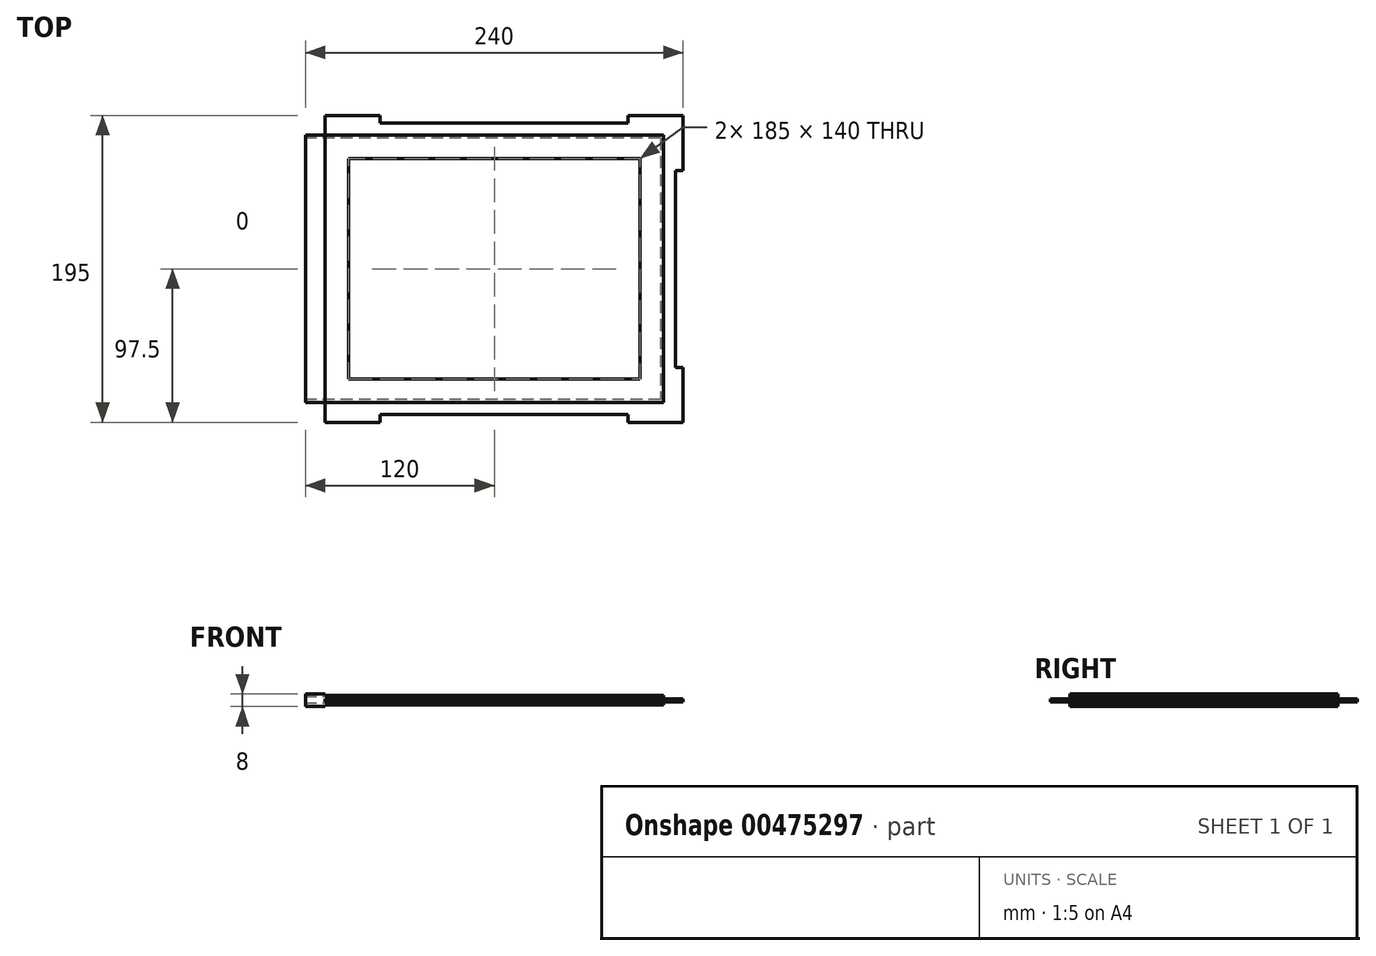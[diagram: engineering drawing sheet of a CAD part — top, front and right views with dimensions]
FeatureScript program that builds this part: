
annotation { "Feature Type Name" : "Feature", "Feature Type Description" : "" }
export const myFeature = defineFeature(function(context is Context, id is Id, definition is map)
    precondition{}
    {
        {
            var Q0;
            Q0=qCreatedBy(makeId("Top.planeOp"),FACE);
            var sketch = newSketch(context, id + "F0", { "sketchPlane" : qUnion([Q0])});
            skLineSegment(sketch, "E0.bottom", {"start": v(92.5, 70) * mm, "end": v(-92.5, 70) * mm});
            skLineSegment(sketch, "E0.top", {"start": v(92.5, -70) * mm, "end": v(-92.5, -70) * mm});
            skLineSegment(sketch, "E0.left", {"start": v(92.5, 70) * mm, "end": v(92.5, -70) * mm});
            skLineSegment(sketch, "E0.right", {"start": v(-92.5, 70) * mm, "end": v(-92.5, -70) * mm});
            skPoint(sketch, "E0.middle", {"position": v(0, 0) * mm});
            skLineSegment(sketch, "E1.bottom", {"start": v(120, 97.5) * mm, "end": v(85, 97.5) * mm});
            skLineSegment(sketch, "E1.top", {"start": v(120, -97.5) * mm, "end": v(85, -97.5) * mm});
            skLineSegment(sketch, "E1.left", {"start": v(120, 97.5) * mm, "end": v(120, 62.5) * mm});
            skLineSegment(sketch, "E1.right", {"start": v(-120, 85) * mm, "end": v(-120, -85) * mm});
            skLineSegment(sketch, "E2.bottom", {"start": v(107.5, -85) * mm, "end": v(-107.5, -85) * mm});
            skLineSegment(sketch, "E2.top", {"start": v(107.5, 85) * mm, "end": v(-107.5, 85) * mm});
            skLineSegment(sketch, "E2.left", {"start": v(107.5, -85) * mm, "end": v(107.5, 85) * mm});
            skLineSegment(sketch, "E2.right", {"start": v(-107.5, -85) * mm, "end": v(-107.5, 85) * mm});
            skLineSegment(sketch, "E3", {"start": v(-107.5, 85) * mm, "end": v(-120, 85) * mm});
            skLineSegment(sketch, "E4", {"start": v(-107.5, 85) * mm, "end": v(-107.5, 97.5) * mm});
            skPoint(sketch, "E5.orphan", {"position": v(-120, 97.5) * mm});
            skLineSegment(sketch, "E6", {"start": v(-107.5, -85) * mm, "end": v(-120, -85) * mm});
            skLineSegment(sketch, "E7", {"start": v(-107.5, -85) * mm, "end": v(-107.5, -97.5) * mm});
            skPoint(sketch, "E8.orphan", {"position": v(-120, -97.5) * mm});
            skLineSegment(sketch, "E9", {"start": v(-72.5, 97.5) * mm, "end": v(-72.5, 92.5) * mm});
            skLineSegment(sketch, "E10", {"start": v(-72.5, 92.5) * mm, "end": v(85, 92.5) * mm});
            skLineSegment(sketch, "E11", {"start": v(85, 92.5) * mm, "end": v(85, 97.5) * mm});
            skLineSegment(sketch, "E12", {"start": v(-72.5, -97.5) * mm, "end": v(-72.5, -92.5) * mm});
            skLineSegment(sketch, "E13", {"start": v(-72.5, -92.5) * mm, "end": v(85, -92.5) * mm});
            skLineSegment(sketch, "E14", {"start": v(85, -92.5) * mm, "end": v(85, -97.5) * mm});
            skLineSegment(sketch, "E15", {"start": v(120, 62.5) * mm, "end": v(115, 62.5) * mm});
            skLineSegment(sketch, "E16", {"start": v(115, 62.5) * mm, "end": v(115, -62.5) * mm});
            skLineSegment(sketch, "E17", {"start": v(115, -62.5) * mm, "end": v(120, -62.5) * mm});
            skLineSegment(sketch, "E18.trimOffspring", {"start": v(-72.5, 97.5) * mm, "end": v(-107.5, 97.5) * mm});
            skLineSegment(sketch, "E19.trimOffspring", {"start": v(120, -62.5) * mm, "end": v(120, -97.5) * mm});
            skLineSegment(sketch, "E20.trimOffspring", {"start": v(-72.5, -97.5) * mm, "end": v(-107.5, -97.5) * mm});
            skSolve(sketch);
        }
        {
            var Q0;
            Q0=makeQuery(id+"F0.imprint","IMPRINT",FACE,{"disambiguationData":[TD([[makeQuery(id+"F0.imprint","IMPRINT",EDGE,{"derivedFrom":sQuery(id+"F0.wireOp",EDGE,"E0.bottom")}),-1.0]])]});
            extrude(context, id + "F1", {"entities" : qUnion([Q0]), "endBound" : BoundingType.SYMMETRIC, "depth" : 6 * mm});
        }
        {
            var Q0;
            Q0=makeQuery(id+"F0.imprint","IMPRINT",FACE,{"disambiguationData":[TD([[makeQuery(id+"F0.imprint","IMPRINT",EDGE,{"derivedFrom":sQuery(id+"F0.wireOp",EDGE,"E1.right")}),1.0]])]});
            extrude(context, id + "F2", {"entities" : qUnion([Q0]), "operationType" : NewBodyOperationType.ADD, "endBound" : BoundingType.SYMMETRIC, "depth" : 8 * mm});
        }
        {
            var Q0;
            Q0=makeQuery(id+"F0.imprint","IMPRINT",FACE,{"disambiguationData":[TD([[makeQuery(id+"F0.imprint","IMPRINT",EDGE,{"derivedFrom":sQuery(id+"F0.wireOp",EDGE,"E1.bottom")}),1.0]])]});
            extrude(context, id + "F3", {"entities" : qUnion([Q0]), "operationType" : NewBodyOperationType.ADD, "endBound" : BoundingType.SYMMETRIC, "depth" : 2 * mm});
        }
        {
            var Q0;
            Q0=makeQuery(id+"F2.opExtrude","SWEPT_FACE",FACE,{"disambiguationData":[OSD([sQuery(id+"F0.wireOp",EDGE,"E1.right")])]});
            var sketch = newSketch(context, id + "F4", { "sketchPlane" : qUnion([Q0])});
            skLineSegment(sketch, "E21.bottom", {"start": v(-83, 2) * mm, "end": v(83, 2) * mm});
            skLineSegment(sketch, "E21.top", {"start": v(-83, -2) * mm, "end": v(83, -2) * mm});
            skLineSegment(sketch, "E21.left", {"start": v(-83, 2) * mm, "end": v(-83, -2) * mm});
            skLineSegment(sketch, "E21.right", {"start": v(83, 2) * mm, "end": v(83, -2) * mm});
            skPoint(sketch, "E21.middle", {"position": v(0, 0) * mm});
            skSolve(sketch);
        }
        {
            var Q0;
            Q0=makeQuery(id+"F4.imprint","IMPRINT",FACE,{"disambiguationData":[TD([[makeQuery(id+"F4.imprint","IMPRINT",EDGE,{"derivedFrom":sQuery(id+"F4.wireOp",EDGE,"E21.bottom")}),-1.0]])]});
            extrude(context, id + "F5", {"entities" : qUnion([Q0]), "operationType" : NewBodyOperationType.REMOVE, "oppositeDirection" : true, "depth" : 225.5 * mm});
        }
    });
